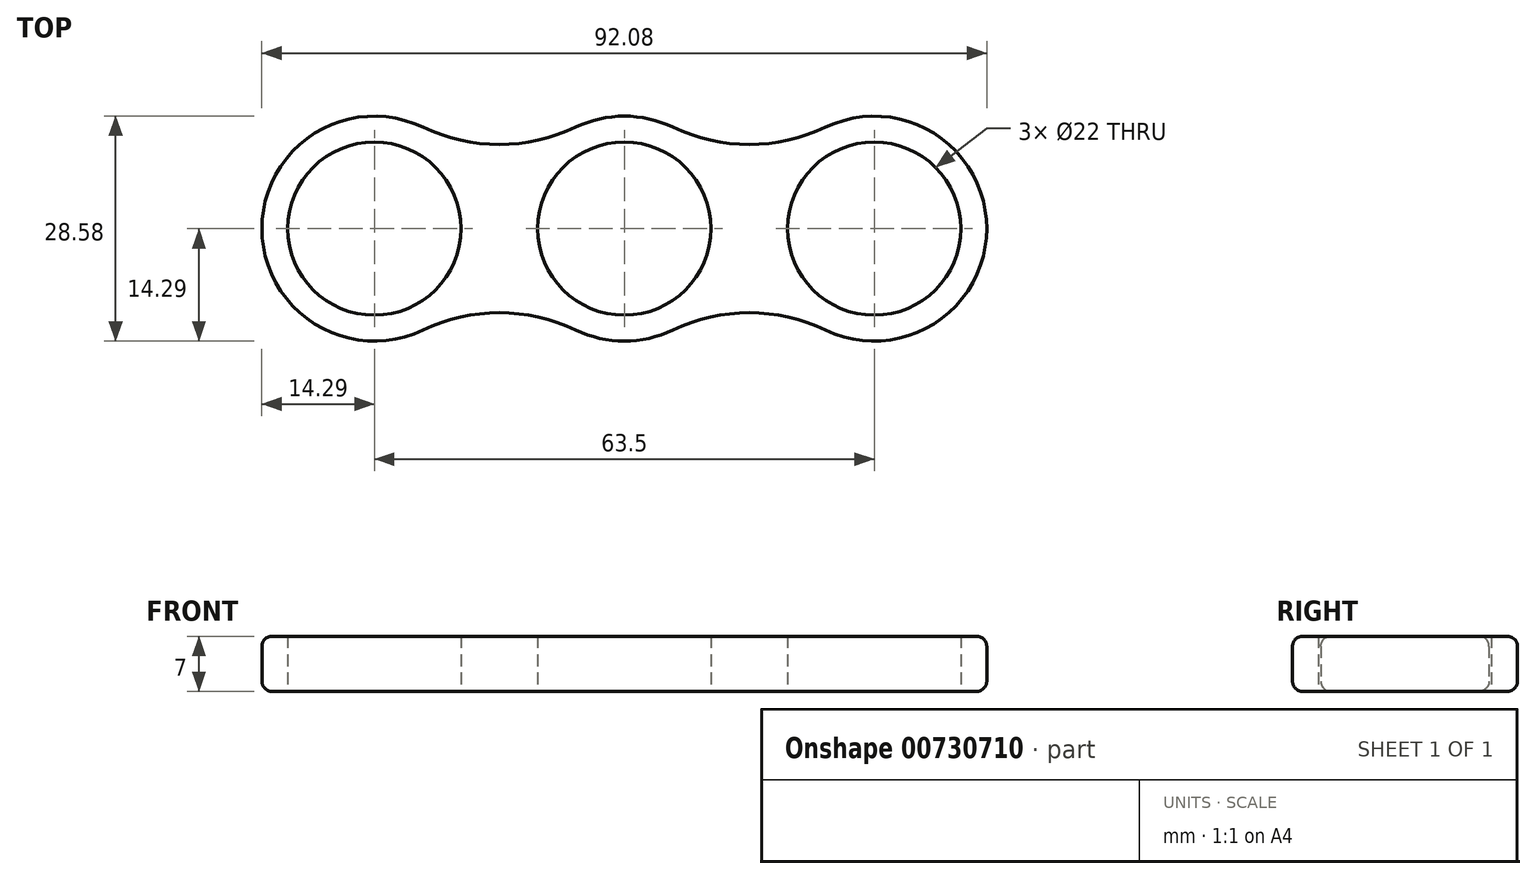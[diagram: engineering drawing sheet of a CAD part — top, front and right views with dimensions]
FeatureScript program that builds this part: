
annotation { "Feature Type Name" : "Feature", "Feature Type Description" : "" }
export const myFeature = defineFeature(function(context is Context, id is Id, definition is map)
    precondition{}
    {
        {
            var Q0;
            Q0=qCreatedBy(makeId("Top.planeOp"),FACE);
            var sketch = newSketch(context, id + "F0", { "sketchPlane" : qUnion([Q0])});
            skCircle(sketch, "E0", {"center": v(0, 0) * mm, "radius": 11 * mm});
            skCircle(sketch, "E1", {"center": v(31.75, 0) * mm, "radius": 11 * mm});
            skCircle(sketch, "E2", {"center": v(0, 0) * mm, "radius": 14.29 * mm});
            skCircle(sketch, "E3", {"center": v(31.75, 0) * mm, "radius": 14.29 * mm});
            skArc(sketch, "E4", {"start": v(6.17, 12.89) * mm, "mid": v(15.88, 10.68) * mm, "end": v(25.58, 12.89) * mm});
            skArc(sketch, "E5.MirrorCS", {"start": v(6.17, -12.89) * mm, "mid": v(15.88, -10.68) * mm, "end": v(25.58, -12.89) * mm});
            skCircle(sketch, "E6.MirrorC", {"center": v(-31.75, 0) * mm, "radius": 11 * mm});
            skArc(sketch, "E7.MirrorCS", {"start": v(-6.17, -12.89) * mm, "mid": v(-15.88, -10.68) * mm, "end": v(-25.58, -12.89) * mm});
            skCircle(sketch, "E8.MirrorC", {"center": v(-31.75, 0) * mm, "radius": 14.29 * mm});
            skArc(sketch, "E9.MirrorCS", {"start": v(-6.17, 12.89) * mm, "mid": v(-15.88, 10.68) * mm, "end": v(-25.58, 12.89) * mm});
            skSolve(sketch);
        }
        {
            var Q0;
            Q0 = qSketchRegion(id + "F0", true);
            extrude(context, id + "F1", {"entities" : qUnion([Q0]), "depth" : 7 * mm, "offsetDistance" : 25.4 * mm});
        }
        {
            var Q0;
            Q0=makeQuery(id+"F1.opExtrude","CAP_EDGE",EDGE,{"disambiguationData":[OSD([sQuery(id+"F0.wireOp",EDGE,"E8.MirrorC")])],"isStart":false});
            var Q1;
            {var subQ0=sQuery(id+"F0.wireOp",EDGE,"E2");Q1=makeQuery(id+"F1.opExtrude","CAP_EDGE",EDGE,{"disambiguationData":[OSD([subQ0]),TDD([makeQuery(id+"F0.imprint","IMPRINT",EDGE,{"disambiguationData":[TD([[makeQuery(id+"F0.imprint","INTERSECT",VERTEX,{"derivedFrom":[subQ0,sQuery(id+"F0.wireOp",EDGE,"E4")]}),-1.0]])],"derivedFrom":subQ0})])],"isStart":true});}
            fillet(context, id + "F2", {"entities" : qUnion([Q0, Q1]), "radius" : 1.27 * mm, "tangentPropagation" : true, "allowEdgeOverflow" : false});
        }
    });
